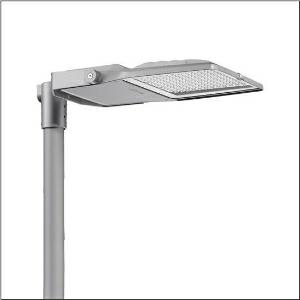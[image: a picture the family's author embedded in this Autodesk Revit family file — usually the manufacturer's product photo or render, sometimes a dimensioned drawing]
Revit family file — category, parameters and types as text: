
# Revit family: floodlight_fl_21_midi___pl52_5xa7781f4d3a_9480
name_source: partatom
category: Lighting Fixtures
units: mm (PartAtom-declared; Revit-internal decimal feet)

## family parameters
Cut with Voids When Loaded = No
Host = Face
Light Source = No
Part Type = Normal
Room Calculation Point = No
Round Connector Dimension = Use Diameter
Shared = No

## types (1)
- --- (1 x LED, 37330 lm, 270.2 W, 4000K)
    Apparent Load = 270 VA
    CIE Flux Codes = 26 60 98 100 100
    Color Rendering = 70
    Color Temperature = 4000K
    Default Elevation = 1800 mm
    Description = Floodlight FL 21 midi, floodlight, primary light control with lens, of PMMA, primary optical cover: protective disc, of toughened safety glass, transparent, light distribution: PL52, light emission: direct distribution, installation type: surface-mounted, LED, High Power LED, rated luminous flux: 37.330lm, luminous efficacy: 138lm/W, light colour: 740, colour temperature: 4000K, control gear: ECG iQ, control: optimised constant luminous flux control (CLO 2.0), Desk-Remote (wireless, voltage-free reading and setting of iQ features in the workshop via application-optimized NFC function/RFID function), Light-Fading, Smart-Wire, Night-Set, Lumen-Switch, Temp-Guard, Auto-Match, with terminal, 6-pole, mains connection: 220..240V, AC, 50/60Hz, start of lifetime: 270W, end of lifetime: 286W, reduction: 138W, luminaire housing, of diecast aluminium, powder-coated, Siteco® metallic grey (DB 702S), corrosivity category C5 according to DIN EN ISO 12944, mast bracket, of steel, galvanised, powder-coated, Siteco® metallic grey (DB 702S), protection rating (complete): IP66, insulation class (complete): insulation class I (protective earthing), certification: CE, protection symbol: D, impact resistance: IK08, permissible operating ambient temperature: -40..+40°C, permissible operating ambient temperature for outdoor applications: -40..+50°C, standard: DIN EN 12944, packaging unit: 1 piece

Light Distribution: PL52
    Height = 76 mm
    Lamp = 1 x LED
    Lamp Light Flux = 37330 lm
    Lamp Power = 270.2 W
    Lamp count = 1
    Length = 657 mm
    Luminous efficacy = 138 lm/W
    Manufacturer = Siteco
    ModVariant = No
    Model = 5XA7781F4D3A
    Number of Poles = 1
    OnlyDefault = Yes
    Power Factor = 1
    Product Name = Floodlight FL 21 midi | PL52
    Product group = floodlight | pylon top
    ProductGroupID = 6101
    Protection Class = Protection class I
    Protection Degree = IP 66
    RLX_Detail_Level = 1
    RlxData = <blob elided: 153765 chars, md5=c70e5bf1>
    Socket = socket
    Standby Power = 0 W
    System Light Flux = 37330 lm
    System Power = 270 W
    Type Comments = factory setting: luminous flux: 100 % | dim-lin: 254 | 620 mA
    Type Image = l_1007123.jpg
    URL = http://relux.com
    VarID = @adj_014355
    Voltage = 0 V
    Weight = 0.00 kg
    Width = 442 mm

## geometry (parser evidence)
native form markers: Blend x4, Sweep x12
no freeform markers — native parametric forms only
